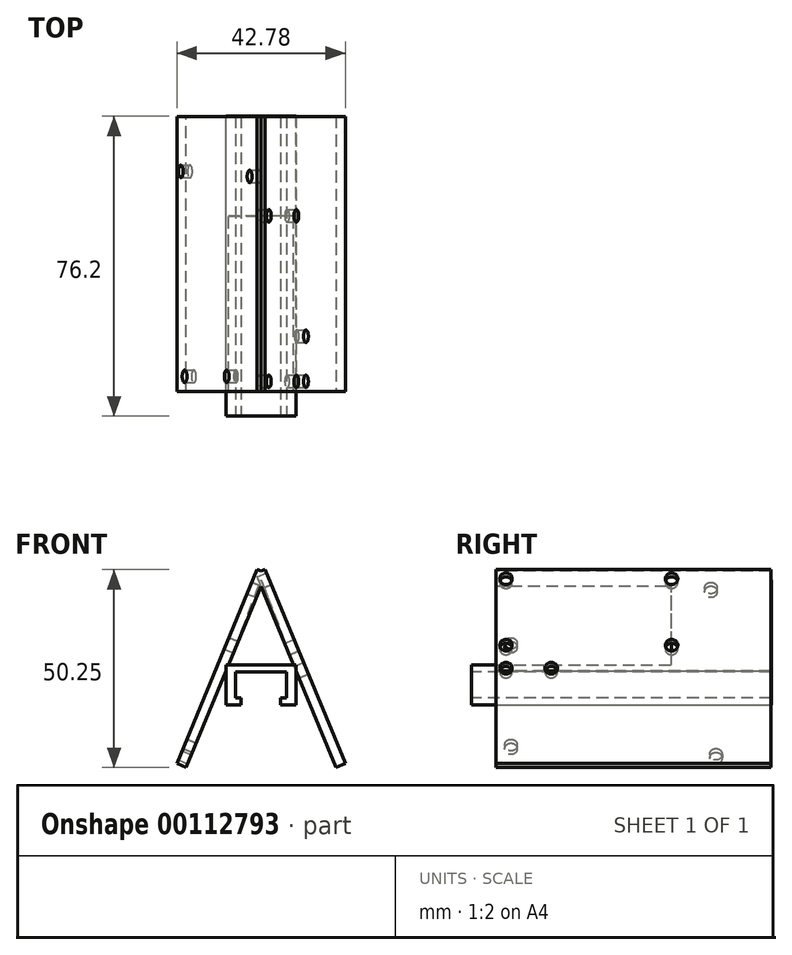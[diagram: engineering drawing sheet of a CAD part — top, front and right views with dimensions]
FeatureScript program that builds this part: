
annotation { "Feature Type Name" : "Feature", "Feature Type Description" : "" }
export const myFeature = defineFeature(function(context is Context, id is Id, definition is map)
    precondition{}
    {
        {
            var Q0;
            Q0=qCreatedBy(makeId("Front.planeOp"),FACE);
            var sketch = newSketch(context, id + "F0", { "sketchPlane" : qUnion([Q0])});
            skLineSegment(sketch, "E0.bottom", {"start": v(8.9, -5.08) * mm, "end": v(-8.9, -5.08) * mm});
            skLineSegment(sketch, "E0.top", {"start": v(8.9, 5.08) * mm, "end": v(-8.9, 5.08) * mm});
            skLineSegment(sketch, "E0.left", {"start": v(8.9, -5.08) * mm, "end": v(8.9, 5.08) * mm});
            skLineSegment(sketch, "E0.right", {"start": v(-8.9, -5.08) * mm, "end": v(-8.9, 5.08) * mm});
            skPoint(sketch, "E0.middle", {"position": v(0, 0) * mm});
            skSolve(sketch);
        }
        {
            var Q0;
            Q0=qSketchRegion(id+"F0",true);
            extrude(context, id + "F1", {"entities" : qUnion([Q0]), "depth" : 76.2 * mm});
        }
        {
            var Q0;
            Q0=makeQuery(id+"F1.opExtrude","CAP_FACE",FACE,{"disambiguationData":[OSD([sQuery(id+"F0.wireOp",EDGE,"E0.bottom"),sQuery(id+"F0.wireOp",EDGE,"E0.top"),sQuery(id+"F0.wireOp",EDGE,"E0.left"),sQuery(id+"F0.wireOp",EDGE,"E0.right")])],"isStart":false});
            var sketch = newSketch(context, id + "F2", { "sketchPlane" : qUnion([Q0])});
            skLineSegment(sketch, "E1.bottom", {"start": v(6.48, -3.3) * mm, "end": v(4.9, -3.3) * mm});
            skLineSegment(sketch, "E1.top", {"start": v(6.48, 3.3) * mm, "end": v(-6.48, 3.3) * mm});
            skLineSegment(sketch, "E1.left", {"start": v(6.48, -3.3) * mm, "end": v(6.48, 3.3) * mm});
            skLineSegment(sketch, "E1.right", {"start": v(-6.48, -3.3) * mm, "end": v(-6.48, 3.3) * mm});
            skPoint(sketch, "E1.middle", {"position": v(0, 0) * mm});
            skLineSegment(sketch, "E2", {"start": v(-5.06, -3.3) * mm, "end": v(-5.06, -5.08) * mm});
            skLineSegment(sketch, "E3", {"start": v(-5.06, -5.08) * mm, "end": v(4.9, -5.08) * mm});
            skLineSegment(sketch, "E4", {"start": v(4.9, -5.08) * mm, "end": v(4.9, -3.3) * mm});
            skLineSegment(sketch, "E5.trimOffspring", {"start": v(-5.06, -3.3) * mm, "end": v(-6.48, -3.3) * mm});
            skSolve(sketch);
        }
        {
            var Q0;
            Q0=qSketchRegion(id+"F2",true);
            extrude(context, id + "F3", {"entities" : qUnion([Q0]), "operationType" : NewBodyOperationType.REMOVE, "endBound" : BoundingType.THROUGH_ALL, "oppositeDirection" : true, "depth" : 25.4 * mm});
        }
        {
            var Q0;
            Q0=qCreatedBy(makeId("Front.planeOp"),FACE);
            var sketch = newSketch(context, id + "F4", { "sketchPlane" : qUnion([Q0])});
            skLineSegment(sketch, "E6.bottom", {"start": v(8.26, -5.08) * mm, "end": v(-8.26, -5.08) * mm});
            skLineSegment(sketch, "E6.top", {"start": v(8.26, 5.08) * mm, "end": v(-8.26, 5.08) * mm});
            skLineSegment(sketch, "E6.left", {"start": v(8.26, -5.08) * mm, "end": v(8.26, 5.08) * mm});
            skLineSegment(sketch, "E6.right", {"start": v(-8.26, -5.08) * mm, "end": v(-8.26, 5.08) * mm});
            skPoint(sketch, "E6.middle", {"position": v(0, 0) * mm});
            skLineSegment(sketch, "E7", {"start": v(0, 25.02) * mm, "end": v(-17.62, -17.53) * mm});
            skLineSegment(sketch, "E8", {"start": v(0, 25.02) * mm, "end": v(18.55, -19.8) * mm});
            skSolve(sketch);
        }
        {
            var Q0;
            Q0=sQuery(id+"F4.wireOp",EDGE,"E7");
            cPlane(context, id + "F5", {"entities" : qUnion([Q0]), "cplaneType" : CPlaneType.LINE_ANGLE, "offset" : 25.4 * mm, "angle" : 0 * degree, "width" : 152.4 * mm, "height" : 152.4 * mm});
        }
        {
            var Q0;
            Q0=sQuery(id+"F4.wireOp",EDGE,"E8");
            cPlane(context, id + "F6", {"entities" : qUnion([Q0]), "cplaneType" : CPlaneType.LINE_ANGLE, "offset" : 25.4 * mm, "angle" : 0 * degree, "width" : 152.4 * mm, "height" : 152.4 * mm});
        }
        {
            var Q0;
            Q0=qCreatedBy(id+"F5.planeOp",FACE);
            var sketch = newSketch(context, id + "F7", { "sketchPlane" : qUnion([Q0])});
            skLineSegment(sketch, "E9.bottom", {"start": v(69.93, -26.67) * mm, "end": v(0.08, -26.67) * mm});
            skLineSegment(sketch, "E9.top", {"start": v(69.93, 26.67) * mm, "end": v(0.08, 26.67) * mm});
            skLineSegment(sketch, "E9.left", {"start": v(69.93, -26.67) * mm, "end": v(69.93, 26.67) * mm});
            skLineSegment(sketch, "E9.right", {"start": v(0.08, -26.67) * mm, "end": v(0.08, 26.67) * mm});
            skPoint(sketch, "E9.middle", {"position": v(35, 0) * mm});
            skSolve(sketch);
        }
        {
            var Q0;
            Q0 = qSketchRegion(id + "F7", true);
            extrude(context, id + "F8", {"entities" : qUnion([Q0]), "operationType" : NewBodyOperationType.ADD, "depth" : 2.54 * mm});
        }
        {
            var Q0;
            Q0=qCreatedBy(id+"F5.planeOp",FACE);
            var sketch = newSketch(context, id + "F9", { "sketchPlane" : qUnion([Q0])});
            skCircle(sketch, "E10", {"center": v(15.32, 21.6) * mm, "radius": 1.59 * mm});
            skCircle(sketch, "E11", {"center": v(14.05, -24.13) * mm, "radius": 1.59 * mm});
            skCircle(sketch, "E12", {"center": v(66.12, 6.35) * mm, "radius": 1.59 * mm});
            skCircle(sketch, "E13", {"center": v(66.12, -21.59) * mm, "radius": 1.59 * mm});
            skSolve(sketch);
        }
        {
            var Q0;
            Q0=qCreatedBy(id+"F6.planeOp",FACE);
            var sketch = newSketch(context, id + "F10", { "sketchPlane" : qUnion([Q0])});
            skLineSegment(sketch, "E14.bottom", {"start": v(0.09, -26.67) * mm, "end": v(69.94, -26.67) * mm});
            skLineSegment(sketch, "E14.top", {"start": v(0.09, 26.67) * mm, "end": v(69.94, 26.67) * mm});
            skLineSegment(sketch, "E14.left", {"start": v(0.09, -26.67) * mm, "end": v(0.09, 26.67) * mm});
            skLineSegment(sketch, "E14.right", {"start": v(69.94, -26.67) * mm, "end": v(69.94, 26.67) * mm});
            skPoint(sketch, "E14.middle", {"position": v(35.01, 0) * mm});
            skSolve(sketch);
        }
        {
            var Q0;
            Q0 = qSketchRegion(id + "F10", true);
            extrude(context, id + "F11", {"entities" : qUnion([Q0]), "operationType" : NewBodyOperationType.ADD, "oppositeDirection" : true, "depth" : 2.54 * mm});
        }
        {
            var Q0;
            Q0=qCreatedBy(makeId("Front.planeOp"),FACE);
            var sketch = newSketch(context, id + "F12", { "sketchPlane" : qUnion([Q0])});
            skLineSegment(sketch, "E15.top", {"start": v(8.26, 5.08) * mm, "end": v(-8.26, 5.08) * mm});
            skPoint(sketch, "E15.middle", {"position": v(0, 0) * mm});
            skLineSegment(sketch, "E16", {"start": v(-8.26, 5.08) * mm, "end": v(0, 26.67) * mm});
            skLineSegment(sketch, "E17", {"start": v(0, 26.67) * mm, "end": v(8.26, 5.08) * mm});
            skPoint(sketch, "E15.bottom.end.orphan", {"position": v(-8.26, -5.08) * mm});
            skPoint(sketch, "E15.bottom.start.orphan", {"position": v(8.26, -5.08) * mm});
            skSolve(sketch);
        }
        {
            var Q0;
            Q0 = qSketchRegion(id + "F12", true);
            extrude(context, id + "F13", {"entities" : qUnion([Q0]), "operationType" : NewBodyOperationType.ADD, "depth" : 25.4 * mm});
        }
        {
            var Q0;
            Q0 = qSketchRegion(id + "F9", true);
            extrude(context, id + "F14", {"entities" : qUnion([Q0]), "operationType" : NewBodyOperationType.REMOVE, "depth" : 2.54 * mm});
        }
        {
            var Q0;
            Q0=makeQuery(id+"F11.opExtrude","CAP_FACE",FACE,{"disambiguationData":[OSD([sQuery(id+"F10.wireOp",EDGE,"E14.bottom"),sQuery(id+"F10.wireOp",EDGE,"E14.top"),sQuery(id+"F10.wireOp",EDGE,"E14.left"),sQuery(id+"F10.wireOp",EDGE,"E14.right")])],"isStart":false});
            var sketch = newSketch(context, id + "F15", { "sketchPlane" : qUnion([Q0])});
            skCircle(sketch, "E18", {"center": v(-67.4, 24.13) * mm, "radius": 1.59 * mm});
            skCircle(sketch, "E19", {"center": v(-25.33, 24.13) * mm, "radius": 1.59 * mm});
            skCircle(sketch, "E20", {"center": v(-67.4, 5.87) * mm, "radius": 1.59 * mm});
            skCircle(sketch, "E21", {"center": v(-25.33, 5.87) * mm, "radius": 1.59 * mm});
            skCircle(sketch, "E22", {"center": v(-67.4, -0.48) * mm, "radius": 1.59 * mm});
            skCircle(sketch, "E23", {"center": v(-55.9, -0.48) * mm, "radius": 1.59 * mm});
            skSolve(sketch);
        }
        {
            var Q0;
            Q0 = qSketchRegion(id + "F15", true);
            extrude(context, id + "F16", {"entities" : qUnion([Q0]), "operationType" : NewBodyOperationType.REMOVE, "oppositeDirection" : true, "depth" : 2.54 * mm});
        }
    });
